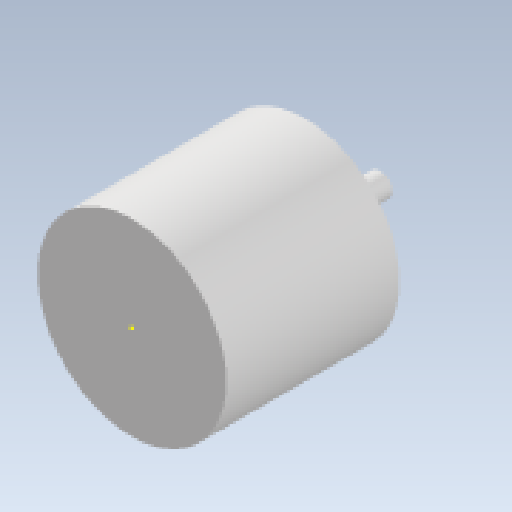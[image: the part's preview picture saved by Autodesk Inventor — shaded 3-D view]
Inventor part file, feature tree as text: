
AUTODESK INVENTOR PART (.ipt)
format: ipt  version: 2023 (Build 270158000, 158)  size: 219,136 bytes
history: native  units: in
note: dims shown in document units (in); Inventor stores cm internally (conversion verified against a paired STEP export)
features: sketch x3, extrude x2
ambient origin geometry x8: Origin, YZ Plane, XZ Plane, XY Plane, X Axis, Y Axis, Z Axis, Center Point
bodies: Solid1 (feature_tree)
feature tree (5):
  extrude  "Extrusion1"  Depth=3.2677in TaperAngle=0.0deg
  extrude  "Extrusion2"  Depth=2.2835in TaperAngle=0.0deg
  sketch  "Sketch4"
  sketch  "Sketch2"  dims[d0=0.315in d1=3.2677in d2=0.0in]
  sketch  "Sketch3"  dims[d3=2.4803in d4=2.2835in d5=0.0in]
